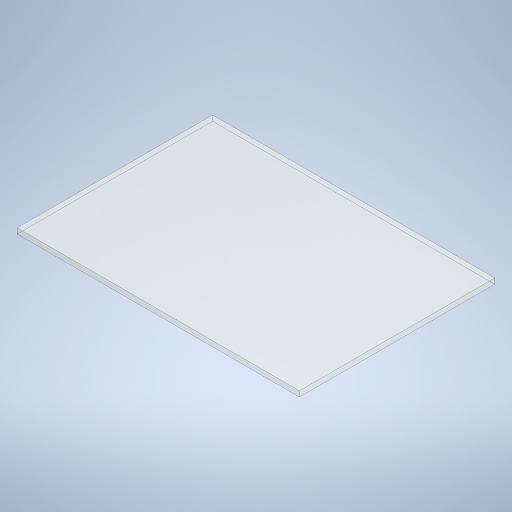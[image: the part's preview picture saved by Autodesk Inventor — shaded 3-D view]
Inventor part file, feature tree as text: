
AUTODESK INVENTOR PART (.ipt)
format: ipt  version: 2024 (Build 280153000, 153)  size: 223,232 bytes
history: native  units: in
note: dims shown in document units (in); Inventor stores cm internally (conversion verified against a paired STEP export)
features: extrude x1, sketch x1
ambient origin geometry x8: Origin, YZ Plane, XZ Plane, XY Plane, X Axis, Y Axis, Z Axis, Center Point
bodies: Solid1 (feature_tree)
feature tree (2):
  extrude  "Extrusion1"  Depth=9.0in
  sketch  "Sketch1"  dims[d0=13.0in d1=9.0in d2=0.25in d3=0.0in]
